FCSTD DOCUMENT  (FreeCAD 0.19R24276 (Git))
Label: pcb-2d
License: All rights reserved
LicenseURL: http://en.wikipedia.org/wiki/All_rights_reserved
objects: Sketcher::SketchObject×1
note: 1 computed .brp shape members not serialized (recipe doc carries the construction recipe); baked Part::Feature solids carry a one-line shape summary decoded from their .brp

FEATURE [Sketcher::SketchObject] Sketch
  FullyConstrained = false
  sketch-geometry (92):
    g0: BSplineCurve PolesCount=2 KnotsCount=2 Degree=1 IsPeriodic=0
    g1: BSplineCurve PolesCount=2 KnotsCount=2 Degree=1 IsPeriodic=0
    g2: BSplineCurve PolesCount=2 KnotsCount=2 Degree=1 IsPeriodic=0
    g3: BSplineCurve PolesCount=2 KnotsCount=2 Degree=1 IsPeriodic=0
    g4: BSplineCurve PolesCount=2 KnotsCount=2 Degree=1 IsPeriodic=0
    g5: BSplineCurve PolesCount=2 KnotsCount=2 Degree=1 IsPeriodic=0
    g6: BSplineCurve PolesCount=2 KnotsCount=2 Degree=1 IsPeriodic=0
    g7: BSplineCurve PolesCount=2 KnotsCount=2 Degree=1 IsPeriodic=0
    g8: BSplineCurve PolesCount=2 KnotsCount=2 Degree=1 IsPeriodic=0
    g9: BSplineCurve PolesCount=2 KnotsCount=2 Degree=1 IsPeriodic=0
    g10: BSplineCurve PolesCount=2 KnotsCount=2 Degree=1 IsPeriodic=0
    g11: BSplineCurve PolesCount=2 KnotsCount=2 Degree=1 IsPeriodic=0
    g12: BSplineCurve PolesCount=7 KnotsCount=4 Degree=2 IsPeriodic=0
    g13: BSplineCurve PolesCount=7 KnotsCount=4 Degree=2 IsPeriodic=0
    g14: BSplineCurve PolesCount=7 KnotsCount=4 Degree=2 IsPeriodic=0
    g15: BSplineCurve PolesCount=7 KnotsCount=4 Degree=2 IsPeriodic=0
    g16: BSplineCurve PolesCount=2 KnotsCount=2 Degree=1 IsPeriodic=0
    g17: BSplineCurve PolesCount=2 KnotsCount=2 Degree=1 IsPeriodic=0
    g18: BSplineCurve PolesCount=2 KnotsCount=2 Degree=1 IsPeriodic=0
    g19: BSplineCurve PolesCount=2 KnotsCount=2 Degree=1 IsPeriodic=0
    g20: BSplineCurve PolesCount=2 KnotsCount=2 Degree=1 IsPeriodic=0
    g21: BSplineCurve PolesCount=2 KnotsCount=2 Degree=1 IsPeriodic=0
    g22: BSplineCurve PolesCount=2 KnotsCount=2 Degree=1 IsPeriodic=0
    g23: BSplineCurve PolesCount=2 KnotsCount=2 Degree=1 IsPeriodic=0
    g24: BSplineCurve PolesCount=2 KnotsCount=2 Degree=1 IsPeriodic=0
    g25: BSplineCurve PolesCount=2 KnotsCount=2 Degree=1 IsPeriodic=0
    g26: BSplineCurve PolesCount=2 KnotsCount=2 Degree=1 IsPeriodic=0
    g27: BSplineCurve PolesCount=2 KnotsCount=2 Degree=1 IsPeriodic=0
    g28: BSplineCurve PolesCount=7 KnotsCount=4 Degree=2 IsPeriodic=0
    g29: BSplineCurve PolesCount=7 KnotsCount=4 Degree=2 IsPeriodic=0
    g30: BSplineCurve PolesCount=7 KnotsCount=4 Degree=2 IsPeriodic=0
    g31: BSplineCurve PolesCount=7 KnotsCount=4 Degree=2 IsPeriodic=0
    g32: BSplineCurve PolesCount=7 KnotsCount=4 Degree=2 IsPeriodic=0
    g33: BSplineCurve PolesCount=7 KnotsCount=4 Degree=2 IsPeriodic=0
    g34: BSplineCurve PolesCount=7 KnotsCount=4 Degree=2 IsPeriodic=0
    g35: BSplineCurve PolesCount=7 KnotsCount=4 Degree=2 IsPeriodic=0
    g36: BSplineCurve PolesCount=7 KnotsCount=4 Degree=2 IsPeriodic=0
    g37: BSplineCurve PolesCount=7 KnotsCount=4 Degree=2 IsPeriodic=0
    g38: BSplineCurve PolesCount=7 KnotsCount=4 Degree=2 IsPeriodic=0
    g39: BSplineCurve PolesCount=7 KnotsCount=4 Degree=2 IsPeriodic=0
    g40: BSplineCurve PolesCount=7 KnotsCount=4 Degree=2 IsPeriodic=0
    g41: BSplineCurve PolesCount=7 KnotsCount=4 Degree=2 IsPeriodic=0
    g42: BSplineCurve PolesCount=2 KnotsCount=2 Degree=1 IsPeriodic=0
    g43: BSplineCurve PolesCount=7 KnotsCount=4 Degree=2 IsPeriodic=0
    g44: BSplineCurve PolesCount=7 KnotsCount=4 Degree=2 IsPeriodic=0
    g45: BSplineCurve PolesCount=7 KnotsCount=4 Degree=2 IsPeriodic=0
    g46: BSplineCurve PolesCount=7 KnotsCount=4 Degree=2 IsPeriodic=0
    g47: BSplineCurve PolesCount=7 KnotsCount=4 Degree=2 IsPeriodic=0
    g48: BSplineCurve PolesCount=7 KnotsCount=4 Degree=2 IsPeriodic=0
    g49: BSplineCurve PolesCount=7 KnotsCount=4 Degree=2 IsPeriodic=0
    g50: BSplineCurve PolesCount=7 KnotsCount=4 Degree=2 IsPeriodic=0
    g51: BSplineCurve PolesCount=7 KnotsCount=4 Degree=2 IsPeriodic=0
    g52: BSplineCurve PolesCount=7 KnotsCount=4 Degree=2 IsPeriodic=0
    g53: BSplineCurve PolesCount=7 KnotsCount=4 Degree=2 IsPeriodic=0
    g54: BSplineCurve PolesCount=7 KnotsCount=4 Degree=2 IsPeriodic=0
    g55: BSplineCurve PolesCount=7 KnotsCount=4 Degree=2 IsPeriodic=0
    g56: BSplineCurve PolesCount=7 KnotsCount=4 Degree=2 IsPeriodic=0
    g57: BSplineCurve PolesCount=7 KnotsCount=4 Degree=2 IsPeriodic=0
    g58: BSplineCurve PolesCount=7 KnotsCount=4 Degree=2 IsPeriodic=0
    g59: BSplineCurve PolesCount=7 KnotsCount=4 Degree=2 IsPeriodic=0
    g60: BSplineCurve PolesCount=7 KnotsCount=4 Degree=2 IsPeriodic=0
    g61: BSplineCurve PolesCount=2 KnotsCount=2 Degree=1 IsPeriodic=0
    g62: BSplineCurve PolesCount=7 KnotsCount=4 Degree=2 IsPeriodic=0
    g63: BSplineCurve PolesCount=7 KnotsCount=4 Degree=2 IsPeriodic=0
    g64: BSplineCurve PolesCount=7 KnotsCount=4 Degree=2 IsPeriodic=0
    g65: BSplineCurve PolesCount=7 KnotsCount=4 Degree=2 IsPeriodic=0
    g66: BSplineCurve PolesCount=7 KnotsCount=4 Degree=2 IsPeriodic=0
    g67: BSplineCurve PolesCount=7 KnotsCount=4 Degree=2 IsPeriodic=0
    g68: BSplineCurve PolesCount=7 KnotsCount=4 Degree=2 IsPeriodic=0
    g69: BSplineCurve PolesCount=7 KnotsCount=4 Degree=2 IsPeriodic=0
    g70: BSplineCurve PolesCount=7 KnotsCount=4 Degree=2 IsPeriodic=0
    g71: BSplineCurve PolesCount=7 KnotsCount=4 Degree=2 IsPeriodic=0
    g72: BSplineCurve PolesCount=7 KnotsCount=4 Degree=2 IsPeriodic=0
    g73: BSplineCurve PolesCount=7 KnotsCount=4 Degree=2 IsPeriodic=0
    g74: BSplineCurve PolesCount=7 KnotsCount=4 Degree=2 IsPeriodic=0
    g75: BSplineCurve PolesCount=7 KnotsCount=4 Degree=2 IsPeriodic=0
    g76: BSplineCurve PolesCount=7 KnotsCount=4 Degree=2 IsPeriodic=0
    g77: BSplineCurve PolesCount=7 KnotsCount=4 Degree=2 IsPeriodic=0
    g78: BSplineCurve PolesCount=7 KnotsCount=4 Degree=2 IsPeriodic=0
    g79: BSplineCurve PolesCount=7 KnotsCount=4 Degree=2 IsPeriodic=0
    g80: BSplineCurve PolesCount=7 KnotsCount=4 Degree=2 IsPeriodic=0
    g81: BSplineCurve PolesCount=7 KnotsCount=4 Degree=2 IsPeriodic=0
    g82: BSplineCurve PolesCount=7 KnotsCount=4 Degree=2 IsPeriodic=0
    g83: BSplineCurve PolesCount=7 KnotsCount=4 Degree=2 IsPeriodic=0
    g84: BSplineCurve PolesCount=7 KnotsCount=4 Degree=2 IsPeriodic=0
    g85: BSplineCurve PolesCount=7 KnotsCount=4 Degree=2 IsPeriodic=0
    g86: BSplineCurve PolesCount=7 KnotsCount=4 Degree=2 IsPeriodic=0
    g87: BSplineCurve PolesCount=7 KnotsCount=4 Degree=2 IsPeriodic=0
    g88: BSplineCurve PolesCount=7 KnotsCount=4 Degree=2 IsPeriodic=0
    g89: BSplineCurve PolesCount=7 KnotsCount=4 Degree=2 IsPeriodic=0
    g90: BSplineCurve PolesCount=7 KnotsCount=4 Degree=2 IsPeriodic=0
    g91: BSplineCurve PolesCount=7 KnotsCount=4 Degree=2 IsPeriodic=0
